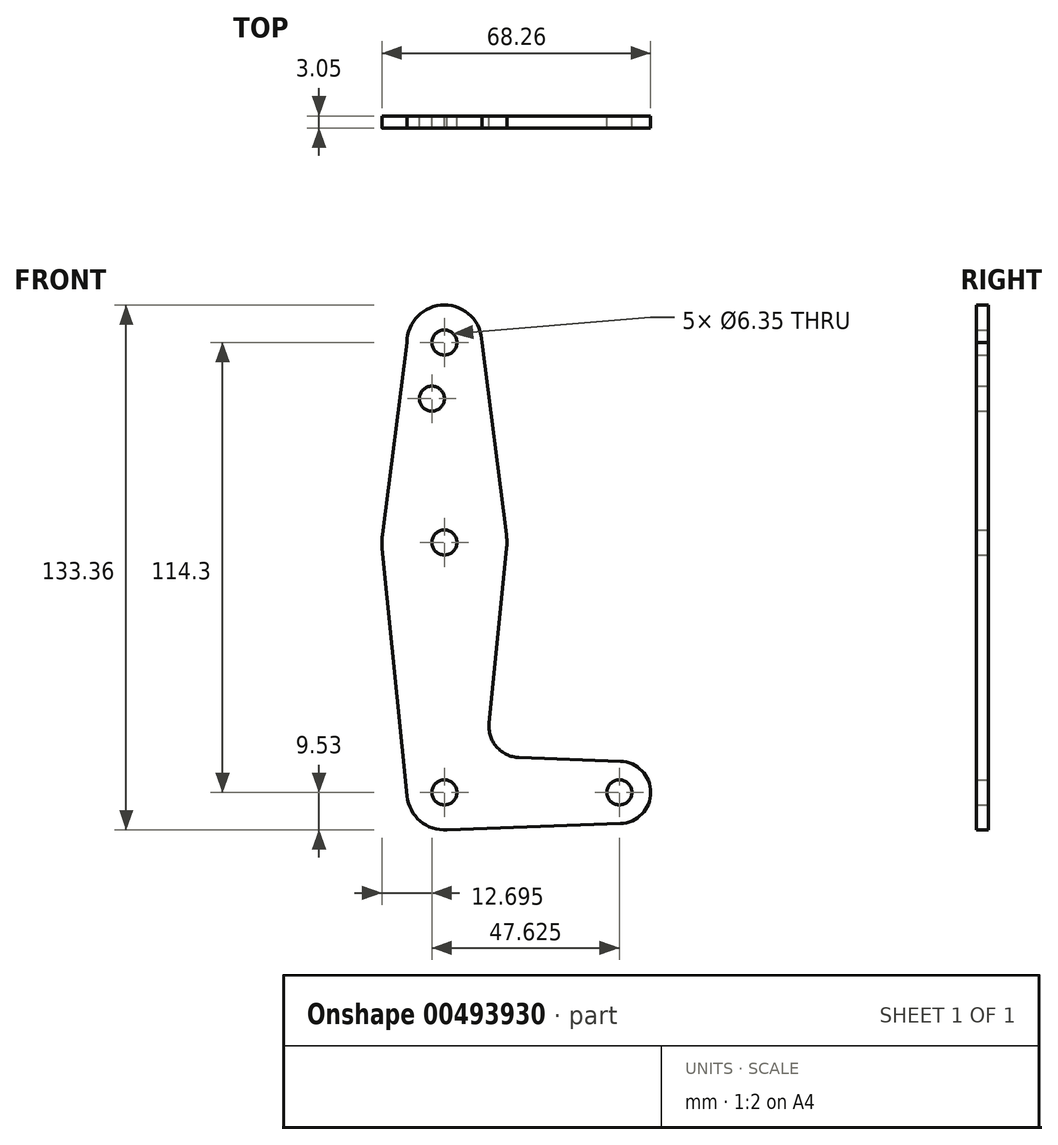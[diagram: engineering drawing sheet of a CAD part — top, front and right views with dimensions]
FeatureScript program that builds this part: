
annotation { "Feature Type Name" : "Feature", "Feature Type Description" : "" }
export const myFeature = defineFeature(function(context is Context, id is Id, definition is map)
    precondition{}
    {
        {
            var Q0;
            Q0=qCreatedBy(makeId("Front.planeOp"),FACE);
            var sketch = newSketch(context, id + "F0", { "sketchPlane" : qUnion([Q0])});
            skLineSegment(sketch, "E0", {"start": v(0, 0) * mm, "end": v(0, 114.3) * mm, "construction": true});
            skLineSegment(sketch, "E1", {"start": v(0, 0) * mm, "end": v(44.45, 0) * mm, "construction": true});
            skCircle(sketch, "E2", {"center": v(0, 114.3) * mm, "radius": 9.53 * mm});
            skCircle(sketch, "E3", {"center": v(0, 0) * mm, "radius": 9.53 * mm});
            skCircle(sketch, "E4", {"center": v(0, 63.5) * mm, "radius": 15.88 * mm});
            skCircle(sketch, "E5", {"center": v(44.45, 0) * mm, "radius": 7.94 * mm});
            skLineSegment(sketch, "E6", {"start": v(9.52, 114.3) * mm, "end": v(15.75, 65.5) * mm});
            skLineSegment(sketch, "E7", {"start": v(-9.52, 114.3) * mm, "end": v(-15.75, 65.5) * mm});
            skLineSegment(sketch, "E8", {"start": v(-15.8, 61.91) * mm, "end": v(-9.48, -0.95) * mm});
            skLineSegment(sketch, "E9", {"start": v(15.8, 61.91) * mm, "end": v(11.34, 17.6) * mm});
            skLineSegment(sketch, "E10", {"start": v(18.97, 8.85) * mm, "end": v(44.73, 7.93) * mm});
            skLineSegment(sketch, "E11", {"start": v(0, -9.53) * mm, "end": v(44.73, -7.93) * mm});
            skCircle(sketch, "E12", {"center": v(-3.18, 100.03) * mm, "radius": 3.18 * mm});
            skCircle(sketch, "E13", {"center": v(0, 114.3) * mm, "radius": 3.18 * mm});
            skCircle(sketch, "E14", {"center": v(0, 63.5) * mm, "radius": 3.18 * mm});
            skCircle(sketch, "E15", {"center": v(0, 0) * mm, "radius": 3.18 * mm});
            skCircle(sketch, "E16", {"center": v(44.45, 0) * mm, "radius": 3.18 * mm});
            skArc(sketch, "E17.filletArc", {"start": v(11.34, 17.6) * mm, "mid": v(13.26, 11.57) * mm, "end": v(18.97, 8.85) * mm});
            skSolve(sketch);
        }
        {
            var Q0;
            Q0 = qSketchRegion(id + "F0", true);
            extrude(context, id + "F1", {"entities" : qUnion([Q0]), "depth" : 3.05 * mm});
        }
    });
